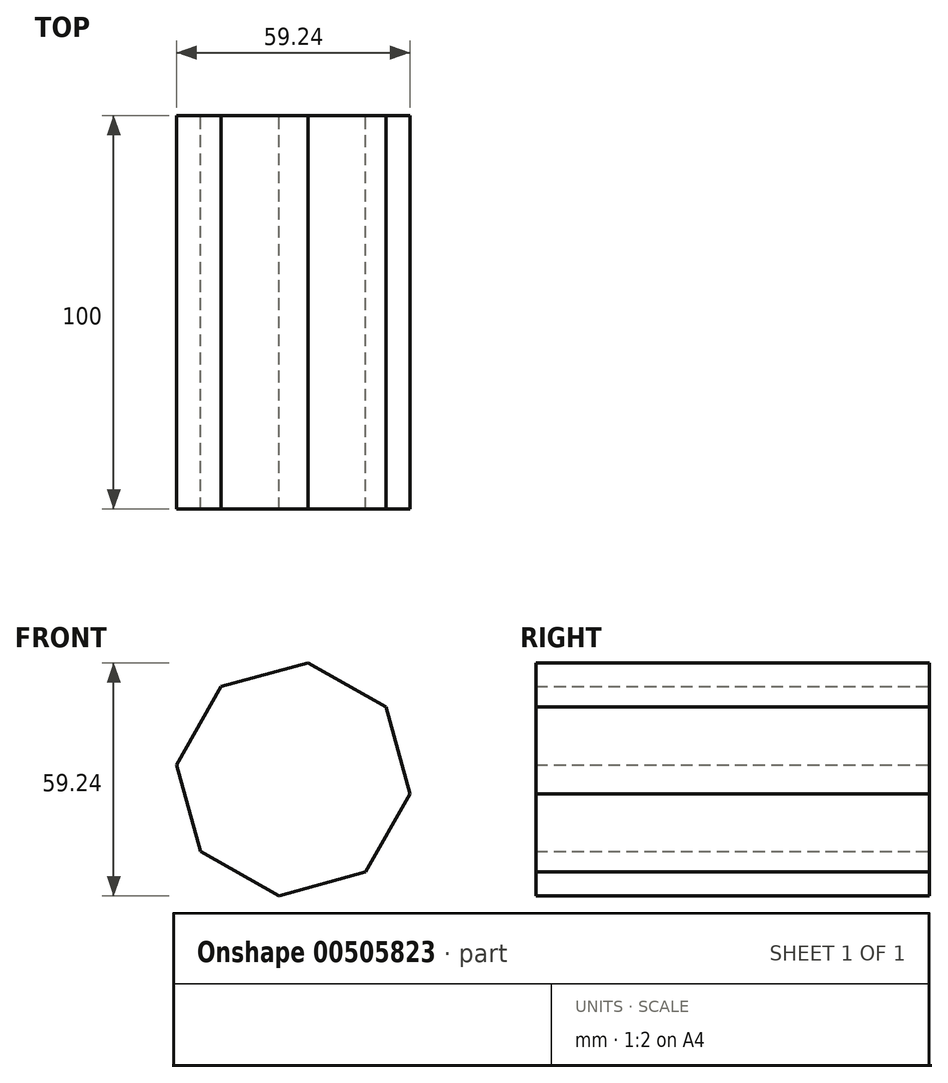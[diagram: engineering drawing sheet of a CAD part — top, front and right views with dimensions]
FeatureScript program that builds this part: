
annotation { "Feature Type Name" : "Feature", "Feature Type Description" : "" }
export const myFeature = defineFeature(function(context is Context, id is Id, definition is map)
    precondition{}
    {
        {
            var Q0;
            Q0=qCreatedBy(makeId("Front.planeOp"),FACE);
            var sketch = newSketch(context, id + "F0", { "sketchPlane" : qUnion([Q0])});
            skCircle(sketch, "E0.cCircle", {"center": v(0, 0) * mm, "radius": 27.58 * mm, "construction": true});
            skLineSegment(sketch, "E0.0", {"start": v(-29.62, 3.69) * mm, "end": v(-18.34, 23.55) * mm});
            skLineSegment(sketch, "E0.1", {"start": v(-18.34, 23.55) * mm, "end": v(3.69, 29.62) * mm});
            skLineSegment(sketch, "E0.2", {"start": v(3.69, 29.62) * mm, "end": v(23.55, 18.34) * mm});
            skLineSegment(sketch, "E0.3", {"start": v(23.55, 18.34) * mm, "end": v(29.62, -3.69) * mm});
            skLineSegment(sketch, "E0.4", {"start": v(29.62, -3.69) * mm, "end": v(18.34, -23.55) * mm});
            skLineSegment(sketch, "E0.5", {"start": v(18.34, -23.55) * mm, "end": v(-3.69, -29.62) * mm});
            skLineSegment(sketch, "E0.6", {"start": v(-3.69, -29.62) * mm, "end": v(-23.55, -18.34) * mm});
            skLineSegment(sketch, "E0.7", {"start": v(-23.55, -18.34) * mm, "end": v(-29.62, 3.69) * mm});
            skPoint(sketch, "E0.0.midPoint", {"position": v(-23.98, 13.62) * mm});
            skSolve(sketch);
        }
        {
            var Q0;
            Q0 = qSketchRegion(id + "F0", true);
            extrude(context, id + "F1", {"entities" : qUnion([Q0]), "endBound" : BoundingType.SYMMETRIC, "depth" : 100 * mm});
        }
    });
